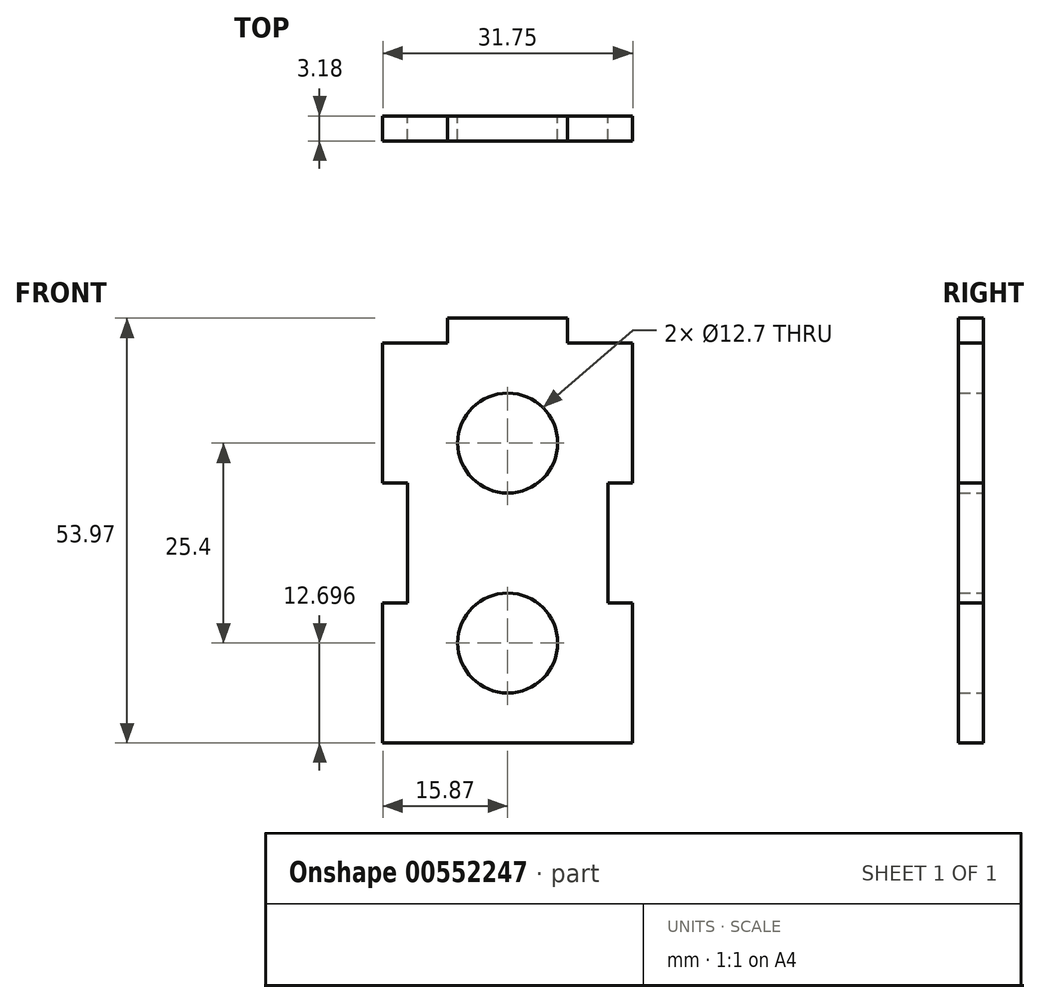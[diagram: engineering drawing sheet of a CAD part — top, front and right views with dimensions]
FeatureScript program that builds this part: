
annotation { "Feature Type Name" : "Feature", "Feature Type Description" : "" }
export const myFeature = defineFeature(function(context is Context, id is Id, definition is map)
    precondition{}
    {
        {
            var Q0;
            Q0=qCreatedBy(makeId("Front.planeOp"),FACE);
            var sketch = newSketch(context, id + "F0", { "sketchPlane" : qUnion([Q0])});
            skLineSegment(sketch, "E0.bottom", {"start": v(-11.66, -28.52) * mm, "end": v(13.74, -28.52) * mm});
            skCircle(sketch, "E1", {"center": v(1.04, 9.58) * mm, "radius": 6.35 * mm});
            skCircle(sketch, "E2", {"center": v(1.04, -15.82) * mm, "radius": 6.35 * mm});
            skLineSegment(sketch, "E3", {"start": v(-6.58, 25.45) * mm, "end": v(-6.58, 22.28) * mm});
            skLineSegment(sketch, "E4", {"start": v(-6.58, 25.45) * mm, "end": v(8.66, 25.45) * mm});
            skLineSegment(sketch, "E5", {"start": v(8.66, 25.45) * mm, "end": v(8.66, 22.28) * mm});
            skLineSegment(sketch, "E6", {"start": v(16.92, 4.5) * mm, "end": v(13.75, 4.5) * mm});
            skLineSegment(sketch, "E7", {"start": v(13.75, 4.5) * mm, "end": v(13.75, -10.74) * mm});
            skLineSegment(sketch, "E8", {"start": v(13.75, -10.74) * mm, "end": v(16.92, -10.74) * mm});
            skLineSegment(sketch, "E9", {"start": v(16.92, 4.5) * mm, "end": v(16.92, 22.28) * mm});
            skLineSegment(sketch, "E10", {"start": v(16.92, 22.28) * mm, "end": v(8.66, 22.28) * mm});
            skLineSegment(sketch, "E11", {"start": v(16.92, -10.74) * mm, "end": v(16.92, -28.52) * mm});
            skLineSegment(sketch, "E12", {"start": v(16.92, -28.52) * mm, "end": v(13.74, -28.52) * mm});
            skLineSegment(sketch, "E13", {"start": v(-11.66, -28.52) * mm, "end": v(-14.83, -28.52) * mm});
            skLineSegment(sketch, "E14", {"start": v(-14.83, -28.52) * mm, "end": v(-14.83, -10.74) * mm});
            skLineSegment(sketch, "E15", {"start": v(-14.83, -10.74) * mm, "end": v(-11.66, -10.74) * mm});
            skLineSegment(sketch, "E16", {"start": v(-11.66, -10.74) * mm, "end": v(-11.66, 4.5) * mm});
            skLineSegment(sketch, "E17", {"start": v(-11.66, 4.5) * mm, "end": v(-14.83, 4.5) * mm});
            skLineSegment(sketch, "E18", {"start": v(-14.83, 4.5) * mm, "end": v(-14.83, 22.28) * mm});
            skLineSegment(sketch, "E19", {"start": v(-14.83, 22.28) * mm, "end": v(-6.58, 22.28) * mm});
            skSolve(sketch);
        }
        {
            var Q0;
            Q0 = qSketchRegion(id + "F0", true);
            extrude(context, id + "F1", {"entities" : qUnion([Q0]), "depth" : 3.17 * mm, "offsetDistance" : 25.4 * mm});
        }
    });
